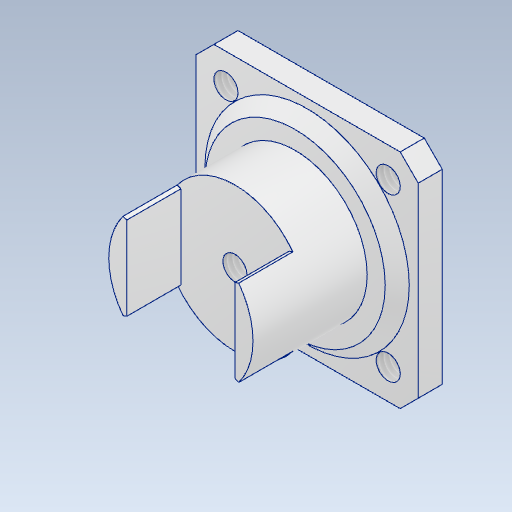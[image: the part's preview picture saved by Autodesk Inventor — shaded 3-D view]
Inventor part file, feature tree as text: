
AUTODESK INVENTOR PART (.ipt)
format: ipt  version: 2024 (Build 280153000, 153)  size: 182,784 bytes
history: native  units: mm
features: other x4, chamfer x2, hole x2, sketch x1
ambient origin geometry x8: Origin, YZ Plane, XZ Plane, XY Plane, X Axis, Y Axis, Z Axis, Center Point
bodies: Body1 (feature_tree)
feature tree (9):
  other  "_bridseye_sketch.ipt"
  chamfer  "面取り2"  Distance=10.0mm
  chamfer  "面取り3"  Distance=2.0mm Angle=45.0deg
  sketch  "スケッチ2"
  hole  "穴2"  [1 undecoded]
  hole  "穴3"  [1 undecoded]
  other  "ソリッド28::_bridseye_sketch.ipt"
  other  "TaggingFeature2"
  other  "front_elbowUnit_links-link2shaft"
note: 2 required parameter values undecoded (feature->parameter linkage not recoverable at this tier; creation-order binding heuristic only, values carry confidence <= 0.55)
